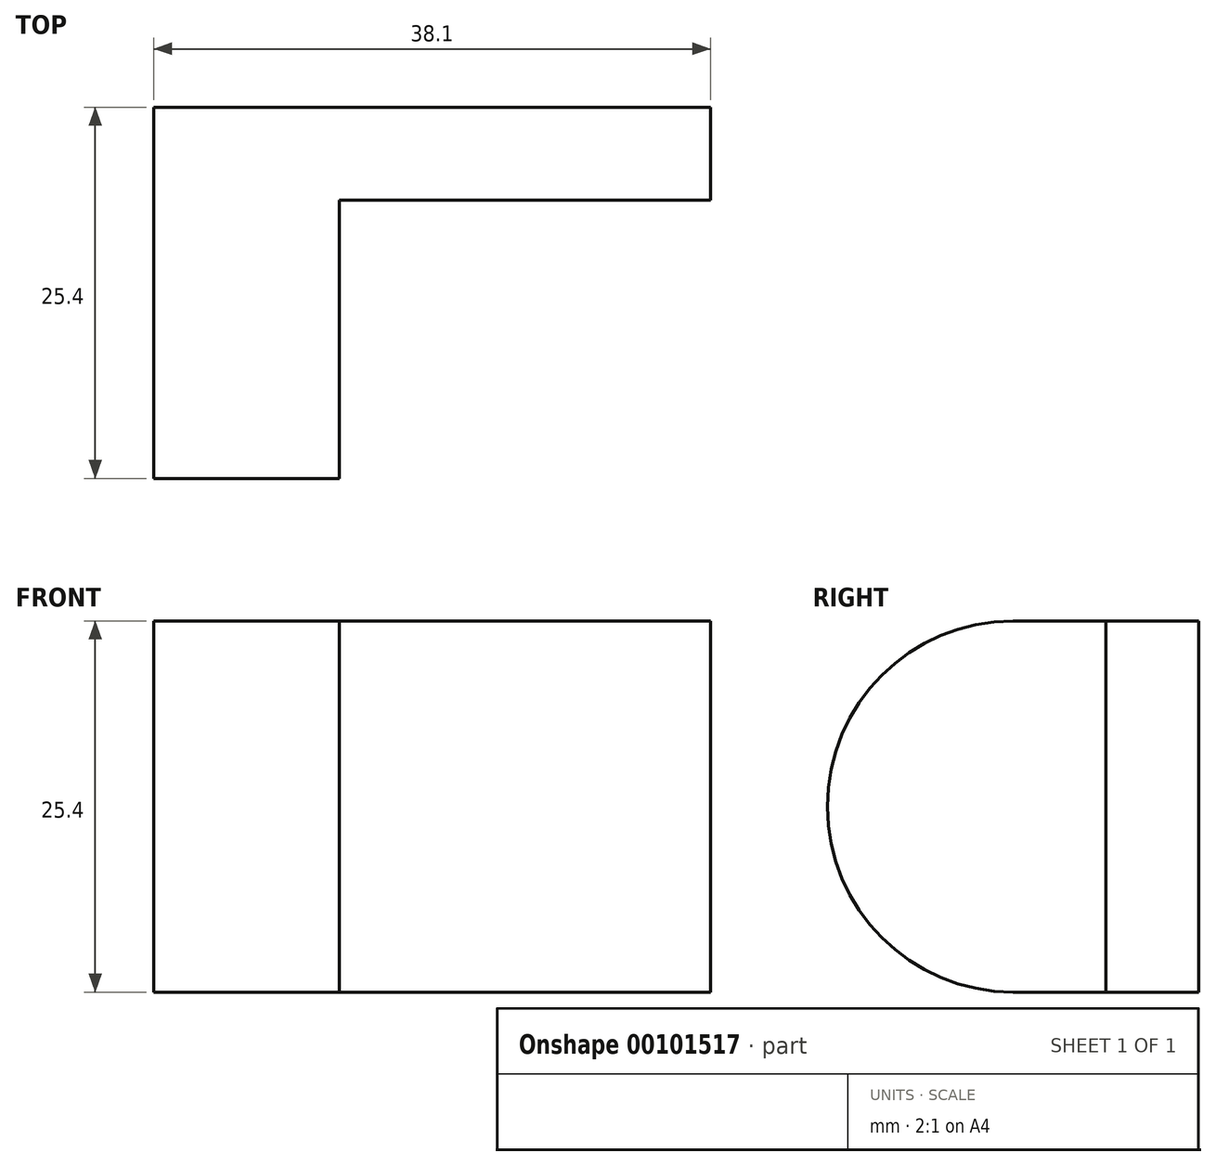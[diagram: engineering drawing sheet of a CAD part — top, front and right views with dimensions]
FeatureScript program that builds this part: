
annotation { "Feature Type Name" : "Feature", "Feature Type Description" : "" }
export const myFeature = defineFeature(function(context is Context, id is Id, definition is map)
    precondition{}
    {
        {
            var Q0;
            Q0=qCreatedBy(makeId("Front.planeOp"),FACE);
            var sketch = newSketch(context, id + "F0", { "sketchPlane" : qUnion([Q0])});
            skLineSegment(sketch, "E0.bottom", {"start": v(0, 0) * mm, "end": v(38.1, 0) * mm});
            skLineSegment(sketch, "E0.top", {"start": v(0, -25.4) * mm, "end": v(38.1, -25.4) * mm});
            skLineSegment(sketch, "E0.left", {"start": v(0, 0) * mm, "end": v(0, -25.4) * mm});
            skLineSegment(sketch, "E0.right", {"start": v(38.1, 0) * mm, "end": v(38.1, -25.4) * mm});
            skSolve(sketch);
        }
        {
            var Q0;
            Q0 = qSketchRegion(id + "F0", true);
            extrude(context, id + "F1", {"entities" : qUnion([Q0]), "depth" : 25.4 * mm});
        }
        {
            var Q0;
            Q0=qCreatedBy(makeId("Top.planeOp"),FACE);
            var sketch = newSketch(context, id + "F2", { "sketchPlane" : qUnion([Q0])});
            skLineSegment(sketch, "E1.bottom", {"start": v(0, 0) * mm, "end": v(12.7, 0) * mm});
            skLineSegment(sketch, "E1.top", {"start": v(0, -25.4) * mm, "end": v(12.7, -25.4) * mm});
            skLineSegment(sketch, "E1.left", {"start": v(0, 0) * mm, "end": v(0, -25.4) * mm});
            skLineSegment(sketch, "E1.right", {"start": v(12.7, 0) * mm, "end": v(12.7, -25.4) * mm});
            skLineSegment(sketch, "E2.bottom", {"start": v(12.7, -25.4) * mm, "end": v(38.1, -25.4) * mm});
            skLineSegment(sketch, "E2.top", {"start": v(12.7, -6.35) * mm, "end": v(38.1, -6.35) * mm});
            skLineSegment(sketch, "E2.left", {"start": v(12.7, -25.4) * mm, "end": v(12.7, -6.35) * mm});
            skLineSegment(sketch, "E2.right", {"start": v(38.1, -25.4) * mm, "end": v(38.1, -6.35) * mm});
            skSolve(sketch);
        }
        {
            var Q0;
            Q0=makeQuery(id+"F2.imprint","IMPRINT",FACE,{"disambiguationData":[TD([[makeQuery(id+"F2.imprint","IMPRINT",EDGE,{"derivedFrom":sQuery(id+"F2.wireOp",EDGE,"E2.bottom")}),1.0]])]});
            extrude(context, id + "F3", {"entities" : qUnion([Q0]), "operationType" : NewBodyOperationType.REMOVE, "endBound" : BoundingType.THROUGH_ALL, "oppositeDirection" : true, "depth" : 25.4 * mm});
        }
        {
            var Q0;
            Q0=qCreatedBy(makeId("Right.planeOp"),FACE);
            var sketch = newSketch(context, id + "F4", { "sketchPlane" : qUnion([Q0])});
            skLineSegment(sketch, "E3.bottom", {"start": v(0, 0) * mm, "end": v(-12.7, 0) * mm});
            skLineSegment(sketch, "E3.top", {"start": v(0, -25.4) * mm, "end": v(-12.7, -25.4) * mm});
            skLineSegment(sketch, "E3.left", {"start": v(0, 0) * mm, "end": v(0, -25.4) * mm});
            skLineSegment(sketch, "E3.right", {"start": v(-12.7, 0) * mm, "end": v(-12.7, -25.4) * mm});
            skArc(sketch, "E4", {"start": v(-12.7, 0) * mm, "mid": v(-25.4, -12.7) * mm, "end": v(-12.7, -25.4) * mm});
            skSolve(sketch);
        }
        {
            var Q0;
            Q0=qCreatedBy(makeId("Right.planeOp"),FACE);
            var sketch = newSketch(context, id + "F5", { "sketchPlane" : qUnion([Q0])});
            skLineSegment(sketch, "E5.bottom", {"start": v(0, 0) * mm, "end": v(-12.7, 0) * mm});
            skLineSegment(sketch, "E5.top", {"start": v(0, -25.4) * mm, "end": v(-12.7, -25.4) * mm});
            skLineSegment(sketch, "E5.left", {"start": v(0, 0) * mm, "end": v(0, -25.4) * mm});
            skLineSegment(sketch, "E5.right", {"start": v(-12.7, 0) * mm, "end": v(-12.7, -25.4) * mm});
            skLineSegment(sketch, "E6.bottom", {"start": v(-12.7, 0) * mm, "end": v(-25.4, 0) * mm});
            skLineSegment(sketch, "E6.top", {"start": v(-12.7, -25.4) * mm, "end": v(-25.4, -25.4) * mm});
            skLineSegment(sketch, "E6.right", {"start": v(-25.4, 0) * mm, "end": v(-25.4, -25.4) * mm});
            skSolve(sketch);
        }
        {
            var Q0;
            Q0=makeQuery(id+"F5.imprint","IMPRINT",FACE,{"disambiguationData":[TD([[makeQuery(id+"F5.imprint","IMPRINT",EDGE,{"derivedFrom":sQuery(id+"F5.wireOp",EDGE,"E6.bottom")}),1.0]])]});
            extrude(context, id + "F6", {"entities" : qUnion([Q0]), "operationType" : NewBodyOperationType.REMOVE, "depth" : 25.4 * mm});
        }
        {
            var Q0;
            Q0=makeQuery(id+"F4.imprint","IMPRINT",FACE,{"disambiguationData":[TD([[makeQuery(id+"F4.imprint","IMPRINT",EDGE,{"derivedFrom":sQuery(id+"F4.wireOp",EDGE,"E3.right")}),-1.0]])]});
            extrude(context, id + "F7", {"entities" : qUnion([Q0]), "operationType" : NewBodyOperationType.ADD, "depth" : 12.7 * mm});
        }
    });
